# Revit family: Domotics-DomesticRanges-GEWISS-SYSTEM_CONTAINER_INSTRUMENT_BLACK
name_source: partatom
category: Apparecchi elettrici
revit_build: Autodesk Revit 2016 (Build: 20161004_0715(x64)
units: mm (PartAtom-declared; Revit-internal decimal feet)

## family parameters
Condiviso = Sì
Host = Superficie
Mantenere orientamento annotazione = No
Punto di calcolo locali = Sì
Quota connettore circolare = Usa diametro
Taglio con vuoti quando caricato = Sì
Tipo di parte = Normale

## types (2) — shared parameters
Catalogue = DOMOTICS
Catalogue Range = SYSTEM - BOXES
Colour = Toner black
Electrocod = 0110
IDF = cf0e1abf-445b-49e9-9535-7f633fbdca32
IDT = f03d5fef-28f3-478f-8201-44e4eefb83d7
Immagine tipo = GW24021.jpg
Larghezza = 181 mm  [stored 0.593832 ft]
Materiale = GEWISS GRIGIO
Produttore = GEWISS S.p.A.
Prospetto di default = 1219 mm
SEO = Panel
Technical sheet = https://www.gewiss.com
URL = https://www.gewiss.com
Version file RFA = 19.4

## per-type parameters (varying)
| type | Description: | Descrizione | EAN code | Modello | Outer dim. LxHxD (mm) |
| GW24021 - 6 gang smoke grey desktop enclosure | 6 gang | 6 GANG SMOKE GREY DESKTOP ENCLOSURE | 8011564002302 | GW24021 | 181x91x60 |
| GW24019 - 4 gang smoke grey desktop enclosure | 4 gang | 4 GANG SMOKE GREY DESKTOP ENCLOSURE | 8011564002289 | GW24019 | 126x91x60 |

note: [stored X ft] marks values corroborated as IEEE doubles in the binary element streams (Revit-internal decimal feet)
